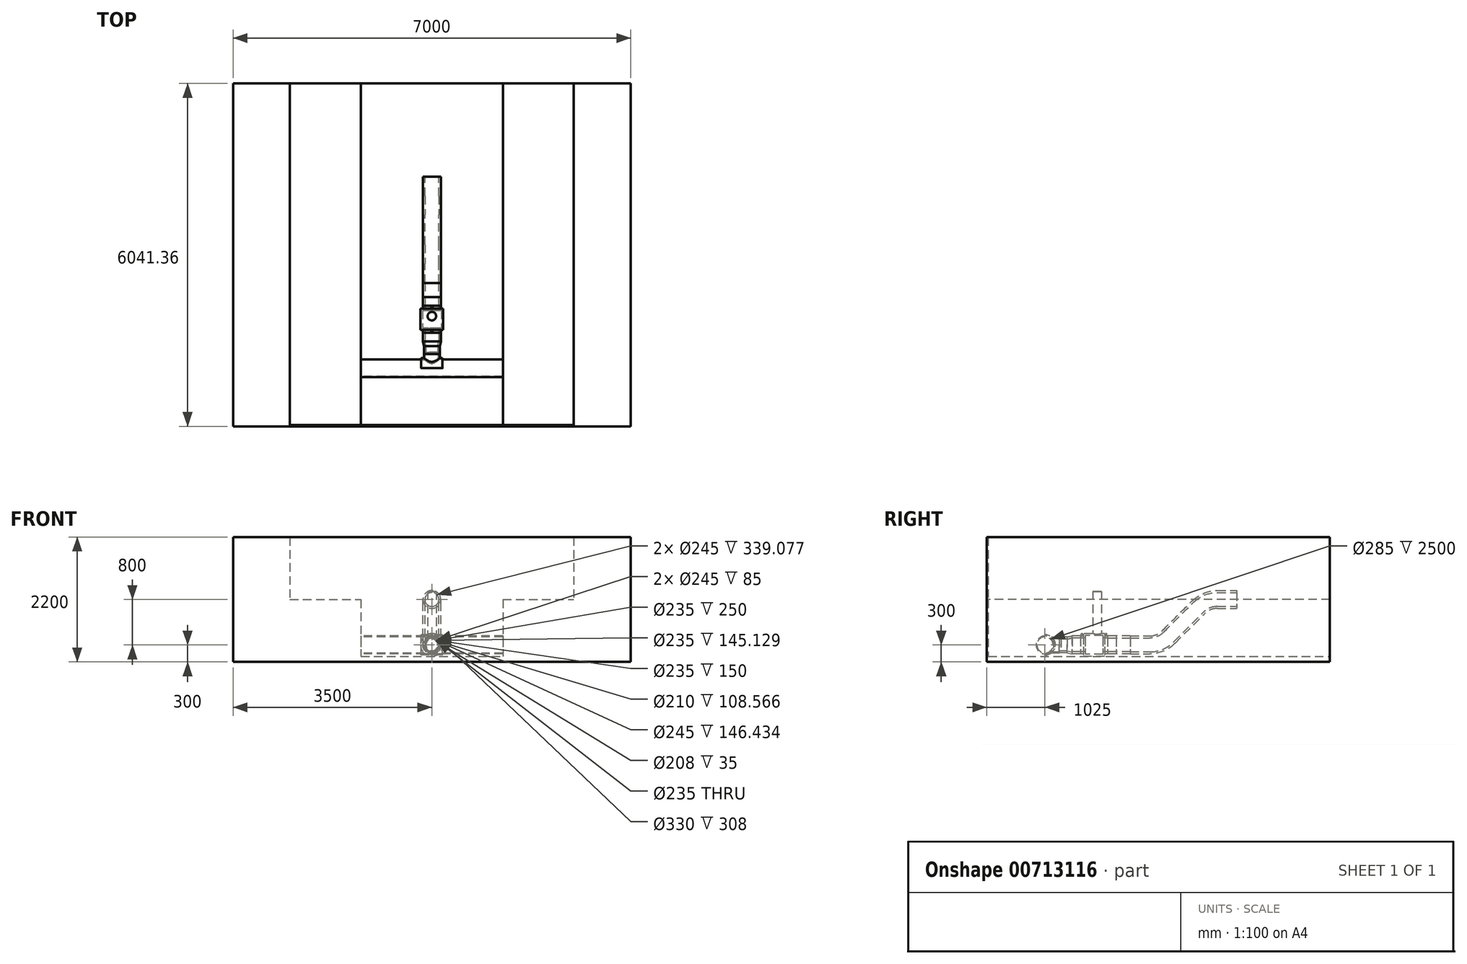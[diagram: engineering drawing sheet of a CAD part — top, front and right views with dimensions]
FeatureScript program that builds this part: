
annotation { "Feature Type Name" : "Feature", "Feature Type Description" : "" }
export const myFeature = defineFeature(function(context is Context, id is Id, definition is map)
    precondition{}
    {
        {
            var Q0;
            Q0=qCreatedBy(makeId("Right.planeOp"),FACE);
            var sketch = newSketch(context, id + "F0", { "sketchPlane" : qUnion([Q0])});
            skCircle(sketch, "E0", {"center": v(0, 0) * mm, "radius": 157.5 * mm});
            skCircle(sketch, "E1", {"center": v(0, 0) * mm, "radius": 142.5 * mm});
            skSolve(sketch);
        }
        {
            var Q0;
            Q0=qSketchRegion(id+"F0",true);
            extrude(context, id + "F1", {"entities" : qUnion([Q0]), "endBound" : BoundingType.SYMMETRIC, "depth" : 5000 * mm, "offsetDistance" : 25 * mm});
        }
        {
            var Q0;
            Q0=qCreatedBy(makeId("Right.planeOp"),FACE);
            var sketch = newSketch(context, id + "F2", { "sketchPlane" : qUnion([Q0])});
            skArc(sketch, "E2", {"start": v(0, -157.5) * mm, "mid": v(157.5, 0) * mm, "end": v(0, 157.5) * mm});
            skArc(sketch, "E3", {"start": v(16.36, -179.25) * mm, "mid": v(180, 0) * mm, "end": v(16.36, 179.25) * mm});
            skLineSegment(sketch, "E4", {"start": v(0, 164.32) * mm, "end": v(0, 157.5) * mm});
            skLineSegment(sketch, "E5.trimOffspring", {"start": v(0, -157.5) * mm, "end": v(0, -164.32) * mm});
            skPoint(sketch, "E6.visualSharp", {"position": v(0, 180) * mm});
            skArc(sketch, "E6.filletArc", {"start": v(16.36, 179.25) * mm, "mid": v(4.89, 175.4) * mm, "end": v(0, 164.32) * mm});
            skPoint(sketch, "E7.visualSharp", {"position": v(0, -180) * mm});
            skArc(sketch, "E7.filletArc", {"start": v(0, -164.32) * mm, "mid": v(4.89, -175.4) * mm, "end": v(16.36, -179.25) * mm});
            skSolve(sketch);
        }
        {
            var Q0;
            Q0=qSketchRegion(id+"F2",true);
            extrude(context, id + "F3", {"entities" : qUnion([Q0]), "endBound" : BoundingType.SYMMETRIC, "depth" : 374 * mm, "offsetDistance" : 25 * mm});
        }
        {
            var Q0;
            Q0=qCreatedBy(makeId("Front.planeOp"),FACE);
            cPlane(context, id + "F4", {"entities" : qUnion([Q0]), "cplaneType" : CPlaneType.OFFSET, "offset" : 250 * mm, "oppositeDirection" : true, "width" : 150 * mm, "height" : 150 * mm});
        }
        {
            var Q0;
            Q0=qCreatedBy(id+"F4.planeOp",FACE);
            var sketch = newSketch(context, id + "F5", { "sketchPlane" : qUnion([Q0])});
            skCircle(sketch, "E8", {"center": v(0, 0) * mm, "radius": 140 * mm});
            skSolve(sketch);
        }
        {
            var Q0;
            Q0=qSketchRegion(id+"F5",true);
            var Q1;
            Q1=makeQuery(id+"F3.opExtrude","SWEPT_FACE",FACE,{"disambiguationData":[OSD([sQuery(id+"F2.wireOp",EDGE,"E3")])]});
            extrude(context, id + "F6", {"entities" : qUnion([Q0]), "operationType" : NewBodyOperationType.ADD, "endBound" : BoundingType.UP_TO_SURFACE, "depth" : 25 * mm, "endBoundEntityFace" : qUnion([Q1]), "offsetDistance" : 25 * mm});
        }
        {
            var Q0;
            Q0=makeQuery(id+"F6.opExtrude","CAP_FACE",FACE,{"disambiguationData":[OSD([sQuery(id+"F5.wireOp",EDGE,"E8")])],"isStart":true});
            var sketch = newSketch(context, id + "F7", { "sketchPlane" : qUnion([Q0])});
            skCircle(sketch, "E9", {"center": v(0, 0) * mm, "radius": 117.5 * mm});
            skSolve(sketch);
        }
        {
            var Q0;
            Q0=qSketchRegion(id+"F7",true);
            extrude(context, id + "F8", {"entities" : qUnion([Q0]), "operationType" : NewBodyOperationType.REMOVE, "oppositeDirection" : true, "depth" : 282 * mm, "offsetDistance" : 25 * mm});
        }
        {
            var Q0;
            Q0=makeQuery(id+"F6.opExtrude","CAP_FACE",FACE,{"disambiguationData":[OSD([sQuery(id+"F5.wireOp",EDGE,"E8")])],"isStart":true});
            var sketch = newSketch(context, id + "F9", { "sketchPlane" : qUnion([Q0])});
            skCircle(sketch, "E10", {"center": v(0, 0) * mm, "radius": 140 * mm});
            skSolve(sketch);
        }
        {
            var Q0;
            Q0=qSketchRegion(id+"F9",true);
            extrude(context, id + "F10", {"entities" : qUnion([Q0]), "depth" : 140 * mm, "offsetDistance" : 25 * mm});
        }
        {
            var Q0;
            Q0=makeQuery(id+"F10.opExtrude","CAP_FACE",FACE,{"disambiguationData":[OSD([sQuery(id+"F9.wireOp",EDGE,"E10"),sQuery(id+"F9.wireOp",EDGE,"hbU6dNIJ-IiIE-Md6K-J93p-wpu8Jisxp6O4")])],"isStart":false});
            var sketch = newSketch(context, id + "F11", { "sketchPlane" : qUnion([Q0])});
            skCircle(sketch, "E11", {"center": v(0, 0) * mm, "radius": 140 * mm});
            skSolve(sketch);
        }
        {
            var Q0;
            Q0=makeQuery(id+"F11.imprint","IMPRINT",FACE,{"disambiguationData":[TD([[makeQuery(id+"F11.imprint","IMPRINT",EDGE,{"derivedFrom":sQuery(id+"F11.wireOp",EDGE,"E11")}),-1.0]])]});
            cPlane(context, id + "F12", {"entities" : qUnion([Q0]), "cplaneType" : CPlaneType.OFFSET, "offset" : 85 * mm, "width" : 150 * mm, "height" : 150 * mm});
        }
        {
            var Q0;
            Q0=qCreatedBy(id+"F12.planeOp",FACE);
            var sketch = newSketch(context, id + "F13", { "sketchPlane" : qUnion([Q0])});
            skCircle(sketch, "E12", {"center": v(0, 0) * mm, "radius": 157.5 * mm});
            skSolve(sketch);
        }
        {
            var Q1;
            Q1=qSketchRegion(id+"F11",true);
            var Q2;
            Q2=qSketchRegion(id+"F13",true);
            loft(context, id + "F14", {"operationType" : NewBodyOperationType.ADD, "sheetProfilesArray" : [{ "sheetProfileEntities" : qUnion([Q1]) }, { "sheetProfileEntities" : qUnion([Q2]) }]});
        }
        {
            var Q0;
            Q0=makeQuery(id+"F14.opLoft","CAP_FACE",FACE,{"disambiguationData":[OSD([makeQuery(id+"F13.imprint","IMPRINT",FACE,{"disambiguationData":[TD([[makeQuery(id+"F13.imprint","IMPRINT",EDGE,{"derivedFrom":sQuery(id+"F13.wireOp",EDGE,"E12")}),1.0]])]})])],"isStart":true});
            var sketch = newSketch(context, id + "F15", { "sketchPlane" : qUnion([Q0])});
            skCircle(sketch, "E13", {"center": v(0, 0) * mm, "radius": 157.5 * mm});
            skSolve(sketch);
        }
        {
            var Q0;
            Q0=qSketchRegion(id+"F15",true);
            extrude(context, id + "F16", {"entities" : qUnion([Q0]), "operationType" : NewBodyOperationType.ADD, "depth" : 150 * mm, "offsetDistance" : 25 * mm});
        }
        {
            var Q0;
            Q0=makeQuery(id+"F16.opExtrude","CAP_FACE",FACE,{"disambiguationData":[OSD([sQuery(id+"F15.wireOp",EDGE,"E13")])],"isStart":false});
            shell(context, id + "F17", {"entities" : qUnion([Q0]), "thickness" : 35 * mm});
        }
        {
            var Q0;
            Q0=qCreatedBy(makeId("Front.planeOp"),FACE);
            var sketch = newSketch(context, id + "F18", { "sketchPlane" : qUnion([Q0])});
            skCircle(sketch, "E14", {"center": v(0, 0) * mm, "radius": 104 * mm});
            skSolve(sketch);
        }
        {
            var Q0;
            Q0=qSketchRegion(id+"F18",true);
            extrude(context, id + "F19", {"entities" : qUnion([Q0]), "operationType" : NewBodyOperationType.REMOVE, "endBound" : BoundingType.THROUGH_ALL, "oppositeDirection" : true, "depth" : 25 * mm, "offsetDistance" : 25 * mm});
        }
        {
            var Q0;
            Q0=makeQuery(id+"F16.opExtrude","CAP_FACE",FACE,{"disambiguationData":[OSD([sQuery(id+"F15.wireOp",EDGE,"E13")])],"isStart":false});
            var sketch = newSketch(context, id + "F20", { "sketchPlane" : qUnion([Q0])});
            skCircle(sketch, "E15", {"center": v(0, 0) * mm, "radius": 157.5 * mm});
            skSolve(sketch);
        }
        {
            var Q0;
            Q0=qSketchRegion(id+"F20",true);
            extrude(context, id + "F21", {"entities" : qUnion([Q0]), "depth" : 50 * mm, "offsetDistance" : 25 * mm});
        }
        {
            var Q0;
            Q0=makeQuery(id+"F21.opExtrude","CAP_FACE",FACE,{"disambiguationData":[OSD([sQuery(id+"F20.wireOp",EDGE,"E15")])],"isStart":false});
            var sketch = newSketch(context, id + "F22", { "sketchPlane" : qUnion([Q0])});
            skCircle(sketch, "E16", {"center": v(0, 0) * mm, "radius": 200 * mm});
            skSolve(sketch);
        }
        {
            var Q0;
            Q0=qSketchRegion(id+"F22",true);
            extrude(context, id + "F23", {"entities" : qUnion([Q0]), "operationType" : NewBodyOperationType.ADD, "depth" : 378 * mm, "offsetDistance" : 25 * mm});
        }
        {
            var Q0;
            Q0=makeQuery(id+"F23.opExtrude","CAP_FACE",FACE,{"disambiguationData":[OSD([sQuery(id+"F22.wireOp",EDGE,"E16")])],"isStart":false});
            var sketch = newSketch(context, id + "F24", { "sketchPlane" : qUnion([Q0])});
            skCircle(sketch, "E17", {"center": v(0, 0) * mm, "radius": 157.5 * mm});
            skSolve(sketch);
        }
        {
            var Q0;
            Q0=qSketchRegion(id+"F24",true);
            extrude(context, id + "F25", {"entities" : qUnion([Q0]), "operationType" : NewBodyOperationType.ADD, "depth" : 50 * mm, "offsetDistance" : 25 * mm});
        }
        {
            var Q0;
            Q0=makeQuery(id+"F25.opExtrude","CAP_FACE",FACE,{"disambiguationData":[OSD([sQuery(id+"F24.wireOp",EDGE,"E17")])],"isStart":false});
            var Q1;
            Q1=makeQuery(id+"F21.opExtrude","CAP_FACE",FACE,{"disambiguationData":[OSD([sQuery(id+"F20.wireOp",EDGE,"E15")])],"isStart":true});
            shell(context, id + "F26", {"entities" : qUnion([Q0, Q1]), "thickness" : 35 * mm});
        }
        {
            var Q0;
            Q0=qCreatedBy(makeId("Top.planeOp"),FACE);
            cPlane(context, id + "F27", {"entities" : qUnion([Q0]), "cplaneType" : CPlaneType.OFFSET, "offset" : 200 * mm, "width" : 150 * mm, "height" : 150 * mm});
        }
        {
            var Q0;
            Q0=qCreatedBy(id+"F27.planeOp",FACE);
            var sketch = newSketch(context, id + "F28", { "sketchPlane" : qUnion([Q0])});
            skCircle(sketch, "E18", {"center": v(0, 917.14) * mm, "radius": 75 * mm});
            skSolve(sketch);
        }
        {
            var Q0;
            Q0=qSketchRegion(id+"F28",true);
            extrude(context, id + "F29", {"entities" : qUnion([Q0]), "operationType" : NewBodyOperationType.ADD, "endBound" : BoundingType.SYMMETRIC, "depth" : 25 * mm, "offsetDistance" : 25 * mm});
        }
        {
            var Q0;
            Q0=qCreatedBy(id+"F27.planeOp",FACE);
            var sketch = newSketch(context, id + "F30", { "sketchPlane" : qUnion([Q0])});
            skCircle(sketch, "E19", {"center": v(0, 650) * mm, "radius": 12.5 * mm});
            skCircle(sketch, "E20", {"center": v(0, 1078) * mm, "radius": 12.5 * mm});
            skSolve(sketch);
        }
        {
            var Q0;
            Q0=qSketchRegion(id+"F30",true);
            var Q1;
            Q1=makeQuery(id+"F21.opExtrude","SWEPT_FACE",FACE,{"disambiguationData":[OSD([sQuery(id+"F20.wireOp",EDGE,"E15")])]});
            extrude(context, id + "F31", {"entities" : qUnion([Q0]), "operationType" : NewBodyOperationType.ADD, "endBound" : BoundingType.UP_TO_SURFACE, "oppositeDirection" : true, "depth" : 25 * mm, "endBoundEntityFace" : qUnion([Q1]), "offsetDistance" : 25 * mm});
        }
        {
            var Q0;
            Q0=makeQuery(id+"F29.opExtrude","CAP_FACE",FACE,{"disambiguationData":[OSD([sQuery(id+"F28.wireOp",EDGE,"E18")])],"isStart":false});
            var sketch = newSketch(context, id + "F32", { "sketchPlane" : qUnion([Q0])});
            skCircle(sketch, "E21", {"center": v(0, 917.14) * mm, "radius": 75 * mm});
            skSolve(sketch);
        }
        {
            var Q0;
            Q0=qSketchRegion(id+"F32",true);
            extrude(context, id + "F33", {"entities" : qUnion([Q0]), "operationType" : NewBodyOperationType.ADD, "depth" : 730 * mm, "offsetDistance" : 25 * mm});
        }
        {
            var Q0;
            Q0=makeQuery(id+"F25.opExtrude","CAP_FACE",FACE,{"disambiguationData":[OSD([sQuery(id+"F24.wireOp",EDGE,"E17")])],"isStart":false});
            var sketch = newSketch(context, id + "F34", { "sketchPlane" : qUnion([Q0])});
            skCircle(sketch, "E22", {"center": v(0, 0) * mm, "radius": 157.5 * mm});
            skCircle(sketch, "E23", {"center": v(0, 0) * mm, "radius": 117.5 * mm});
            skSolve(sketch);
        }
        {
            var Q0;
            Q0=qSketchRegion(id+"F34",true);
            extrude(context, id + "F35", {"entities" : qUnion([Q0]), "depth" : 150 * mm, "offsetDistance" : 25 * mm});
        }
        {
            var Q0;
            Q0=makeQuery(id+"F35.opExtrude","CAP_FACE",FACE,{"disambiguationData":[OSD([sQuery(id+"F34.wireOp",EDGE,"E22"),sQuery(id+"F34.wireOp",EDGE,"E23")])],"isStart":false});
            var sketch = newSketch(context, id + "F36", { "sketchPlane" : qUnion([Q0])});
            skCircle(sketch, "E24", {"center": v(0, 0) * mm, "radius": 157.5 * mm});
            skCircle(sketch, "E25", {"center": v(0, 0) * mm, "radius": 117.5 * mm});
            skSolve(sketch);
        }
        {
            var Q0;
            Q0=qSketchRegion(id+"F36",true);
            extrude(context, id + "F37", {"entities" : qUnion([Q0]), "depth" : 250 * mm, "offsetDistance" : 25 * mm});
        }
        {
            var Q0;
            Q0=makeQuery(id+"F37.opExtrude","CAP_FACE",FACE,{"disambiguationData":[OSD([sQuery(id+"F36.wireOp",EDGE,"E24"),sQuery(id+"F36.wireOp",EDGE,"E25")])],"isStart":false});
            var sketch = newSketch(context, id + "F38", { "sketchPlane" : qUnion([Q0])});
            skCircle(sketch, "E26", {"center": v(0, 0) * mm, "radius": 157.5 * mm});
            skSolve(sketch);
        }
        {
            var Q0;
            Q0=qCreatedBy(makeId("Right.planeOp"),FACE);
            var sketch = newSketch(context, id + "F39", { "sketchPlane" : qUnion([Q0])});
            skLineSegment(sketch, "E27", {"start": v(1503, 0) * mm, "end": v(1842.08, 0) * mm});
            skLineSegment(sketch, "E28", {"start": v(2176.54, 138.54) * mm, "end": v(2416.3, 378.3) * mm});
            skLineSegment(sketch, "E29", {"start": v(2416.3, 378.3) * mm, "end": v(2459.7, 421.7) * mm});
            skLineSegment(sketch, "E30", {"start": v(2459.7, 421.7) * mm, "end": v(2699.46, 661.46) * mm});
            skLineSegment(sketch, "E31", {"start": v(3033.92, 800) * mm, "end": v(3373, 800) * mm});
            skPoint(sketch, "E32.visualSharp", {"position": v(2038, 0) * mm});
            skArc(sketch, "E32.filletArc", {"start": v(1842.08, 0) * mm, "mid": v(2023.09, 36) * mm, "end": v(2176.54, 138.54) * mm});
            skPoint(sketch, "E33.visualSharp", {"position": v(2838, 800) * mm});
            skArc(sketch, "E33.filletArc", {"start": v(3033.92, 800) * mm, "mid": v(2852.91, 764) * mm, "end": v(2699.46, 661.46) * mm});
            skSolve(sketch);
        }
        {
            var Q0;
            Q0=qSketchRegion(id+"F38",true);
            var Q1;
            Q1=qConstructionFilter(qBodyType(qCreatedBy(id+"F39",EDGE),BodyType.WIRE),ConstructionObject.NO);
            sweep(context, id + "F40", {"profiles" : qUnion([Q0]), "path" : qUnion([Q1])});
        }
        {
            var Q0;
            Q0=makeQuery(id+"F40.opSweep","CAP_FACE",FACE,{"disambiguationData":[OSD([sQuery(id+"F38.wireOp",EDGE,"E26"),sQuery(id+"F39.wireOp",VERTEX,"E27.start")])],"isStart":true});
            var Q1;
            Q1=makeQuery(id+"F40.opSweep","CAP_FACE",FACE,{"disambiguationData":[OSD([sQuery(id+"F38.wireOp",EDGE,"E26"),sQuery(id+"F39.wireOp",VERTEX,"E31.end")])],"isStart":false});
            shell(context, id + "F41", {"entities" : qUnion([Q0, Q1]), "thickness" : 35 * mm});
        }
        {
            var Q0;
            Q0=qCreatedBy(makeId("Top.planeOp"),FACE);
            cPlane(context, id + "F42", {"entities" : qUnion([Q0]), "cplaneType" : CPlaneType.OFFSET, "offset" : 200 * mm, "oppositeDirection" : true, "width" : 150 * mm, "height" : 150 * mm});
        }
        {
            var Q0;
            Q0=qCreatedBy(id+"F42.planeOp",FACE);
            var sketch = newSketch(context, id + "F43", { "sketchPlane" : qUnion([Q0])});
            skLineSegment(sketch, "E34.bottom", {"start": v(-2500, 5016.36) * mm, "end": v(2500, 5016.36) * mm});
            skLineSegment(sketch, "E34.top", {"start": v(-2500, -1000) * mm, "end": v(2500, -1000) * mm});
            skLineSegment(sketch, "E34.left", {"start": v(-2500, 5016.36) * mm, "end": v(-2500, -1000) * mm});
            skLineSegment(sketch, "E34.right", {"start": v(2500, 5016.36) * mm, "end": v(2500, -1000) * mm});
            skSolve(sketch);
        }
        {
            var Q0;
            Q0 = qSketchRegion(id + "F43", true);
            extrude(context, id + "F44", {"entities" : qUnion([Q0]), "operationType" : NewBodyOperationType.ADD, "oppositeDirection" : true, "depth" : 100 * mm, "offsetDistance" : 25 * mm});
        }
        {
            var Q0;
            Q0=makeQuery(id+"F44.opExtrude","CAP_FACE",FACE,{"disambiguationData":[OSD([sQuery(id+"F43.wireOp",EDGE,"E34.bottom"),sQuery(id+"F43.wireOp",EDGE,"E34.top"),sQuery(id+"F43.wireOp",EDGE,"E34.left"),sQuery(id+"F43.wireOp",EDGE,"E34.right")])],"isStart":true});
            var sketch = newSketch(context, id + "F45", { "sketchPlane" : qUnion([Q0])});
            skLineSegment(sketch, "E35.bottom", {"start": v(-2500, -1000) * mm, "end": v(-1250, -1000) * mm});
            skLineSegment(sketch, "E35.top", {"start": v(-2500, 5016.36) * mm, "end": v(-1250, 5016.36) * mm});
            skLineSegment(sketch, "E35.left", {"start": v(-2500, -1000) * mm, "end": v(-2500, 5016.36) * mm});
            skLineSegment(sketch, "E35.right", {"start": v(-1250, -1000) * mm, "end": v(-1250, 5016.36) * mm});
            skLineSegment(sketch, "E36.bottom", {"start": v(2500, -1000) * mm, "end": v(1250, -1000) * mm});
            skLineSegment(sketch, "E36.top", {"start": v(2500, 5016.36) * mm, "end": v(1250, 5016.36) * mm});
            skLineSegment(sketch, "E36.left", {"start": v(2500, -1000) * mm, "end": v(2500, 5016.36) * mm});
            skLineSegment(sketch, "E36.right", {"start": v(1250, -1000) * mm, "end": v(1250, 5016.36) * mm});
            skSolve(sketch);
        }
        {
            var Q0;
            Q0 = qSketchRegion(id + "F45", true);
            extrude(context, id + "F46", {"entities" : qUnion([Q0]), "operationType" : NewBodyOperationType.ADD, "depth" : 1000 * mm, "offsetDistance" : 25 * mm});
        }
        {
            var Q0;
            Q0=makeQuery(id+"F46.boolean.opBoolean","MERGE",FACE,{"derivedFrom":[makeQuery(id+"F44.opExtrude","SWEPT_FACE",FACE,{"disambiguationData":[OSD([sQuery(id+"F43.wireOp",EDGE,"E34.top")])]}),makeQuery(id+"F46.opExtrude","SWEPT_FACE",FACE,{"disambiguationData":[OSD([sQuery(id+"F45.wireOp",EDGE,"E35.bottom")])]}),makeQuery(id+"F46.opExtrude","SWEPT_FACE",FACE,{"disambiguationData":[OSD([sQuery(id+"F45.wireOp",EDGE,"E36.bottom")])]})]});
            var sketch = newSketch(context, id + "F47", { "sketchPlane" : qUnion([Q0])});
            skLineSegment(sketch, "E37.bottom", {"start": v(-2500, 800) * mm, "end": v(2500, 800) * mm});
            skLineSegment(sketch, "E37.top", {"start": v(-2500, -300) * mm, "end": v(2500, -300) * mm});
            skLineSegment(sketch, "E37.left", {"start": v(-2500, 800) * mm, "end": v(-2500, -300) * mm});
            skLineSegment(sketch, "E37.right", {"start": v(2500, 800) * mm, "end": v(2500, -300) * mm});
            skSolve(sketch);
        }
        {
            var Q0;
            Q0 = qSketchRegion(id + "F47", true);
            extrude(context, id + "F48", {"entities" : qUnion([Q0]), "operationType" : NewBodyOperationType.ADD, "depth" : 25 * mm, "offsetDistance" : 25 * mm});
        }
        {
            var Q0;
            Q0=makeQuery(id+"F48.boolean.opBoolean","MERGE",FACE,{"derivedFrom":[makeQuery(id+"F46.opExtrude","CAP_FACE",FACE,{"disambiguationData":[OSD([sQuery(id+"F45.wireOp",EDGE,"E35.bottom"),sQuery(id+"F45.wireOp",EDGE,"E35.top"),sQuery(id+"F45.wireOp",EDGE,"E35.left"),sQuery(id+"F45.wireOp",EDGE,"E35.right")])],"isStart":false}),makeQuery(id+"F46.opExtrude","CAP_FACE",FACE,{"disambiguationData":[OSD([sQuery(id+"F45.wireOp",EDGE,"E36.bottom"),sQuery(id+"F45.wireOp",EDGE,"E36.top"),sQuery(id+"F45.wireOp",EDGE,"E36.left"),sQuery(id+"F45.wireOp",EDGE,"E36.right")])],"isStart":false}),makeQuery(id+"F48.opExtrude","SWEPT_FACE",FACE,{"disambiguationData":[OSD([sQuery(id+"F47.wireOp",EDGE,"E37.bottom")])]})]});
            var sketch = newSketch(context, id + "F49", { "sketchPlane" : qUnion([Q0])});
            skLineSegment(sketch, "E38.bottom", {"start": v(2500, 5016.36) * mm, "end": v(3500, 5016.36) * mm});
            skLineSegment(sketch, "E38.top", {"start": v(2500, -1025) * mm, "end": v(3500, -1025) * mm});
            skLineSegment(sketch, "E38.left", {"start": v(2500, 5016.36) * mm, "end": v(2500, -1025) * mm});
            skLineSegment(sketch, "E38.right", {"start": v(3500, 5016.36) * mm, "end": v(3500, -1025) * mm});
            skLineSegment(sketch, "E39.bottom", {"start": v(-2500, 5016.36) * mm, "end": v(-3500, 5016.36) * mm});
            skLineSegment(sketch, "E39.top", {"start": v(-2500, -1025) * mm, "end": v(-3500, -1025) * mm});
            skLineSegment(sketch, "E39.left", {"start": v(-2500, 5016.36) * mm, "end": v(-2500, -1025) * mm});
            skLineSegment(sketch, "E39.right", {"start": v(-3500, 5016.36) * mm, "end": v(-3500, -1025) * mm});
            skSolve(sketch);
        }
        {
            var Q0;
            Q0 = qSketchRegion(id + "F49", true);
            extrude(context, id + "F50", {"entities" : qUnion([Q0]), "operationType" : NewBodyOperationType.ADD, "endBound" : BoundingType.SYMMETRIC, "depth" : 2200 * mm, "offsetDistance" : 25 * mm});
        }
        {
            var Q0;
            Q0=makeQuery(id+"F50.boolean.opBoolean","MERGE",FACE,{"derivedFrom":[makeQuery(id+"F48.opExtrude","CAP_FACE",FACE,{"disambiguationData":[OSD([sQuery(id+"F47.wireOp",EDGE,"E37.bottom"),sQuery(id+"F47.wireOp",EDGE,"E37.top"),sQuery(id+"F47.wireOp",EDGE,"E37.left"),sQuery(id+"F47.wireOp",EDGE,"E37.right")])],"isStart":false}),makeQuery(id+"F50.opExtrude","SWEPT_FACE",FACE,{"disambiguationData":[OSD([sQuery(id+"F49.wireOp",EDGE,"E38.top")])]}),makeQuery(id+"F50.opExtrude","SWEPT_FACE",FACE,{"disambiguationData":[OSD([sQuery(id+"F49.wireOp",EDGE,"E39.top")])]})]});
            var sketch = newSketch(context, id + "F51", { "sketchPlane" : qUnion([Q0])});
            skLineSegment(sketch, "E40.bottom", {"start": v(-3500, 1900) * mm, "end": v(3500, 1900) * mm});
            skLineSegment(sketch, "E40.top", {"start": v(-3500, -300) * mm, "end": v(3500, -300) * mm});
            skLineSegment(sketch, "E40.left", {"start": v(-3500, 1900) * mm, "end": v(-3500, -300) * mm});
            skLineSegment(sketch, "E40.right", {"start": v(3500, 1900) * mm, "end": v(3500, -300) * mm});
            skSolve(sketch);
        }
        {
            var Q0;
            {var subQ1=sQuery(id+"F47.wireOp",EDGE,"E37.bottom");Q0=makeQuery(id+"F51.imprint","IMPRINT",FACE,{"disambiguationData":[TD([[makeQuery(id+"F51.imprint","IMPRINT",EDGE,{"derivedFrom":makeQuery(id+"F48.opExtrude","CAP_EDGE",EDGE,{"disambiguationData":[OSD([subQ1])],"isStart":false})}),1.0]])]});}
            extrude(context, id + "F52", {"entities" : qUnion([Q0]), "operationType" : NewBodyOperationType.ADD, "oppositeDirection" : true, "depth" : 25 * mm, "offsetDistance" : 25 * mm});
        }
    });
